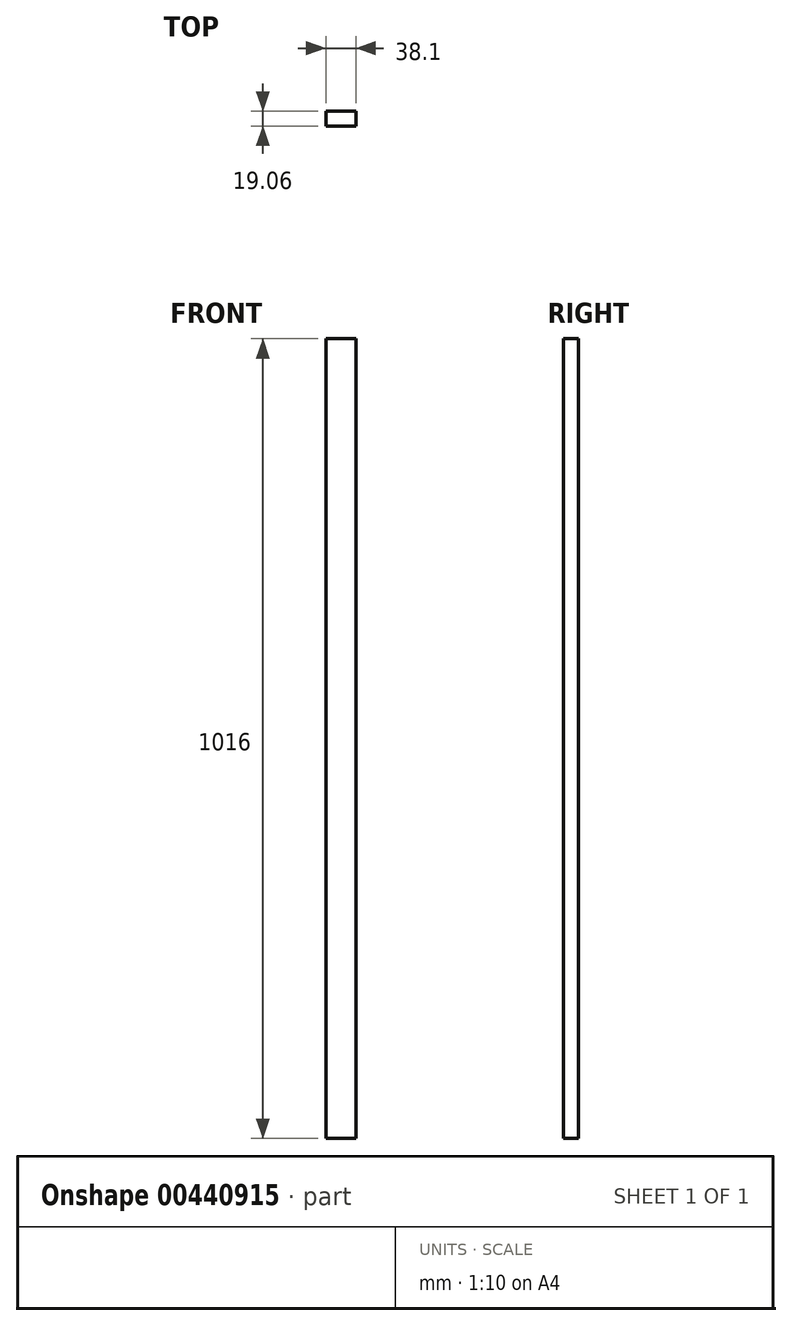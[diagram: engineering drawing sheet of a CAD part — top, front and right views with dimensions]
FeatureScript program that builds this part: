
annotation { "Feature Type Name" : "Feature", "Feature Type Description" : "" }
export const myFeature = defineFeature(function(context is Context, id is Id, definition is map)
    precondition{}
    {
        {
            var Q0;
            Q0=qCreatedBy(makeId("Top.planeOp"),FACE);
            var sketch = newSketch(context, id + "F0", { "sketchPlane" : qUnion([Q0])});
            skLineSegment(sketch, "E0.bottom", {"start": v(19.05, 9.53) * mm, "end": v(-19.05, 9.53) * mm});
            skLineSegment(sketch, "E0.top", {"start": v(19.05, -9.53) * mm, "end": v(-19.05, -9.53) * mm});
            skLineSegment(sketch, "E0.left", {"start": v(19.05, 9.53) * mm, "end": v(19.05, -9.53) * mm});
            skLineSegment(sketch, "E0.right", {"start": v(-19.05, 9.53) * mm, "end": v(-19.05, -9.53) * mm});
            skPoint(sketch, "E0.middle", {"position": v(0, 0) * mm});
            skSolve(sketch);
        }
        {
            var Q0;
            Q0 = qSketchRegion(id + "F0", true);
            extrude(context, id + "F1", {"entities" : qUnion([Q0]), "depth" : 1016 * mm});
        }
    });
